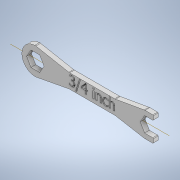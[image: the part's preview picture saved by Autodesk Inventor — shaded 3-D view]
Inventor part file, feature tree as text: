
AUTODESK INVENTOR PART (.ipt)
format: ipt  version: 2020.2 (Build 242310000, 310)  size: 325,632 bytes
history: native  units: in
note: dims shown in document units (in); Inventor stores cm internally (conversion verified against a paired STEP export)
features: extrude x2, fillet x2, sketch x2
ambient origin geometry x8: Origin, YZ Plane, XZ Plane, XY Plane, X Axis, Y Axis, Z Axis, Center Point
bodies: Body1 (feature_tree)
feature tree (6):
  extrude  "Extrusion2"  Depth=0.25in
  fillet  "Fillet1"  Radius=0.25in
  fillet  "Fillet2"  Radius=0.25in
  extrude  "Extrusion3"  Depth=0.0312in
  sketch  "Sketch2"  dims[d23=0.375in d24=0.25in d26=0.25in d27=0.25in]
  sketch  "Sketch3"  dims[d28=0.0in d29=0.0312in d30=0.25in d31=0.0in d32=0.0in]
